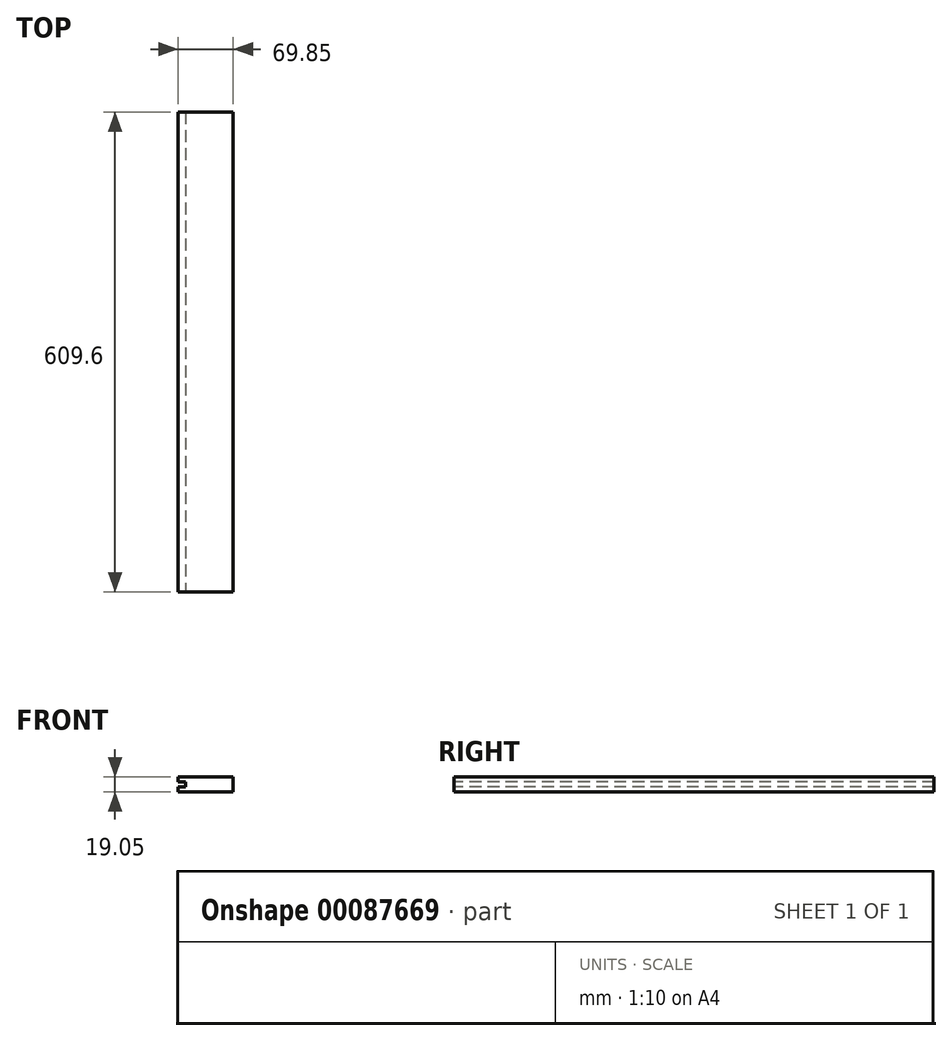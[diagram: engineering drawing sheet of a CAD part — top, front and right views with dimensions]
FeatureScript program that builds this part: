
annotation { "Feature Type Name" : "Feature", "Feature Type Description" : "" }
export const myFeature = defineFeature(function(context is Context, id is Id, definition is map)
    precondition{}
    {
        {
            var Q0;
            Q0=qCreatedBy(makeId("Front.planeOp"),FACE);
            var sketch = newSketch(context, id + "F0", { "sketchPlane" : qUnion([Q0])});
            skLineSegment(sketch, "E0.bottom", {"start": v(0, 0) * mm, "end": v(-69.85, 0) * mm});
            skLineSegment(sketch, "E0.top", {"start": v(0, 19.05) * mm, "end": v(-69.85, 19.05) * mm});
            skLineSegment(sketch, "E0.left", {"start": v(0, 0) * mm, "end": v(0, 19.05) * mm});
            skLineSegment(sketch, "E0.right", {"start": v(-69.85, 0) * mm, "end": v(-69.85, 19.05) * mm});
            skSolve(sketch);
        }
        {
            var Q0;
            Q0 = qSketchRegion(id + "F0", true);
            extrude(context, id + "F1", {"entities" : qUnion([Q0]), "endBound" : BoundingType.SYMMETRIC, "depth" : 609.6 * mm});
        }
        {
            var Q0;
            Q0=makeQuery(id+"F1.opExtrude","CAP_FACE",FACE,{"disambiguationData":[OSD([sQuery(id+"F0.wireOp",EDGE,"E0.bottom"),sQuery(id+"F0.wireOp",EDGE,"E0.top"),sQuery(id+"F0.wireOp",EDGE,"E0.left"),sQuery(id+"F0.wireOp",EDGE,"E0.right")])],"isStart":false});
            var sketch = newSketch(context, id + "F2", { "sketchPlane" : qUnion([Q0])});
            skLineSegment(sketch, "E1.bottom", {"start": v(-69.85, 12.7) * mm, "end": v(-60.33, 12.7) * mm});
            skLineSegment(sketch, "E1.top", {"start": v(-69.85, 6.35) * mm, "end": v(-60.33, 6.35) * mm});
            skLineSegment(sketch, "E1.left", {"start": v(-69.85, 12.7) * mm, "end": v(-69.85, 6.35) * mm});
            skLineSegment(sketch, "E1.right", {"start": v(-60.33, 12.7) * mm, "end": v(-60.33, 6.35) * mm});
            skSolve(sketch);
        }
        {
            var Q0;
            Q0 = qSketchRegion(id + "F2", true);
            extrude(context, id + "F3", {"entities" : qUnion([Q0]), "operationType" : NewBodyOperationType.REMOVE, "endBound" : BoundingType.THROUGH_ALL, "oppositeDirection" : true, "depth" : 25.4 * mm});
        }
    });
